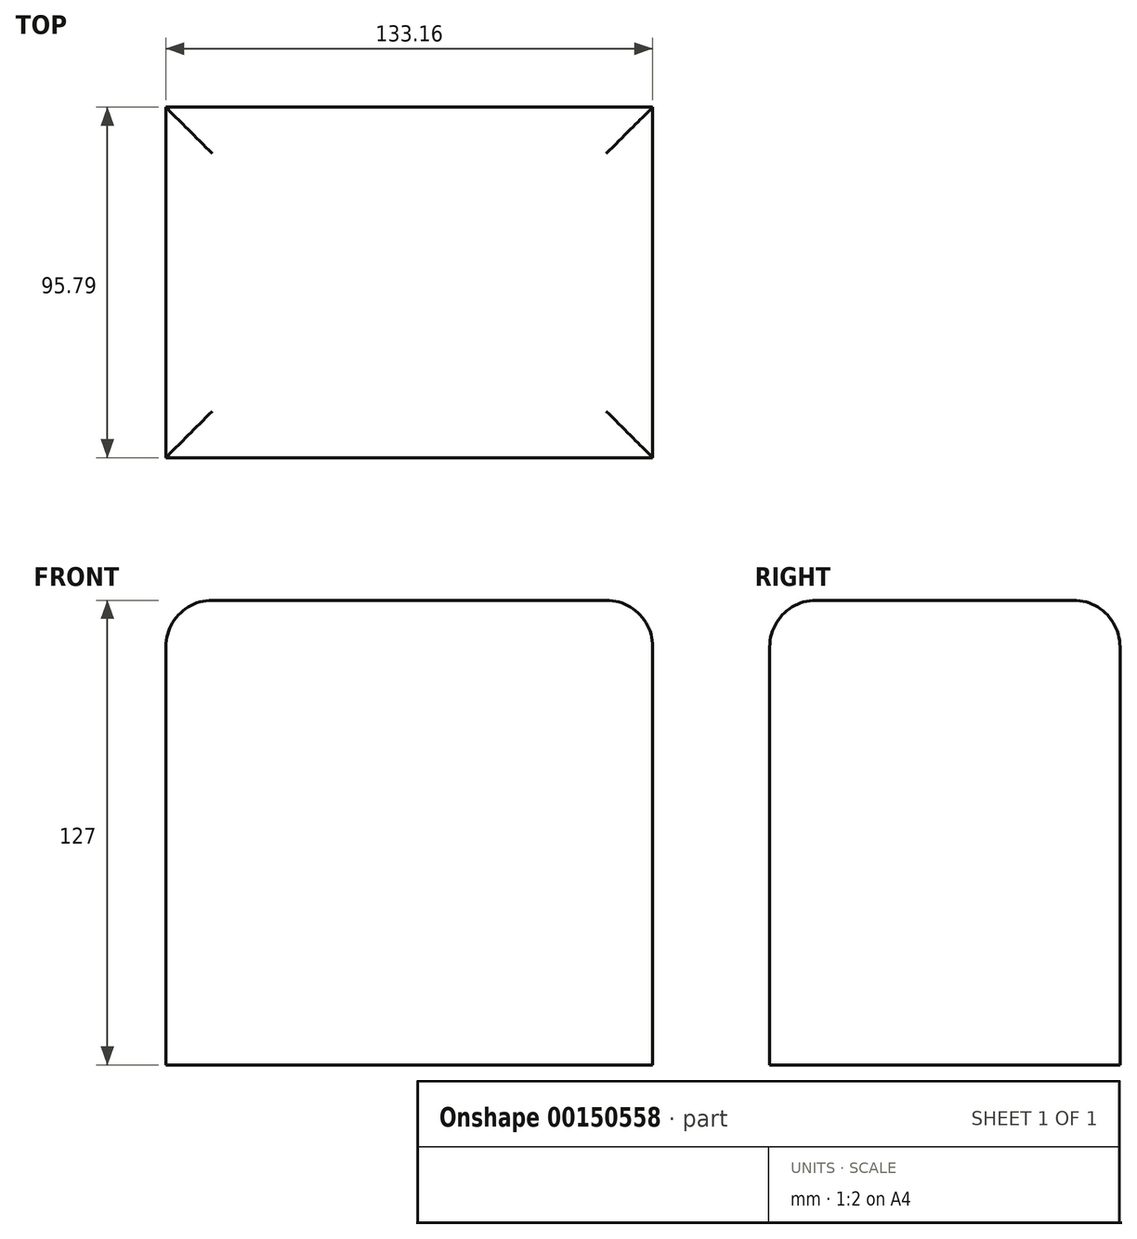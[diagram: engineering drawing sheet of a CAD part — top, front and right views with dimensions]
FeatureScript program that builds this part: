
annotation { "Feature Type Name" : "Feature", "Feature Type Description" : "" }
export const myFeature = defineFeature(function(context is Context, id is Id, definition is map)
    precondition{}
    {
        {
            var Q0;
            Q0=qCreatedBy(makeId("Top.planeOp"),FACE);
            var sketch = newSketch(context, id + "F0", { "sketchPlane" : qUnion([Q0])});
            skLineSegment(sketch, "E0.bottom", {"start": v(-91.65, 65.47) * mm, "end": v(41.5, 65.47) * mm});
            skLineSegment(sketch, "E0.top", {"start": v(-91.65, -30.32) * mm, "end": v(41.5, -30.32) * mm});
            skLineSegment(sketch, "E0.left", {"start": v(-91.65, 65.47) * mm, "end": v(-91.65, -30.32) * mm});
            skLineSegment(sketch, "E0.right", {"start": v(41.5, 65.47) * mm, "end": v(41.5, -30.32) * mm});
            skSolve(sketch);
        }
        {
            var Q0;
            Q0=makeQuery(id+"F0.imprint","IMPRINT",FACE,{"disambiguationData":[TD([[makeQuery(id+"F0.imprint","IMPRINT",EDGE,{"derivedFrom":sQuery(id+"F0.wireOp",EDGE,"E0.bottom")}),-1.0]])]});
            var Q1;
            Q1 = qConstructionFilter(qBodyType(qCreatedBy(id + "F0" ,EDGE), BodyType.WIRE), ConstructionObject.NO);
            extrude(context, id + "F1", {"entities" : qUnion([Q0]), "surfaceEntities" : qUnion([Q1]), "depth" : 127 * mm});
        }
        {
            var Q0;
            Q0=makeQuery(id+"F1.opExtrude","CAP_EDGE",EDGE,{"disambiguationData":[OSD([sQuery(id+"F0.wireOp",EDGE,"E0.left")])],"isStart":false});
            var Q1;
            Q1=makeQuery(id+"F1.opExtrude","CAP_EDGE",EDGE,{"disambiguationData":[OSD([sQuery(id+"F0.wireOp",EDGE,"E0.bottom")])],"isStart":false});
            var Q2;
            Q2=makeQuery(id+"F1.opExtrude","CAP_EDGE",EDGE,{"disambiguationData":[OSD([sQuery(id+"F0.wireOp",EDGE,"E0.right")])],"isStart":false});
            var Q3;
            Q3=makeQuery(id+"F1.opExtrude","CAP_EDGE",EDGE,{"disambiguationData":[OSD([sQuery(id+"F0.wireOp",EDGE,"E0.top")])],"isStart":false});
            fillet(context, id + "F2", {"entities" : qUnion([Q0, Q1, Q2, Q3]), "radius" : 12.7 * mm, "tangentPropagation" : true, "allowEdgeOverflow" : false});
        }
    });
